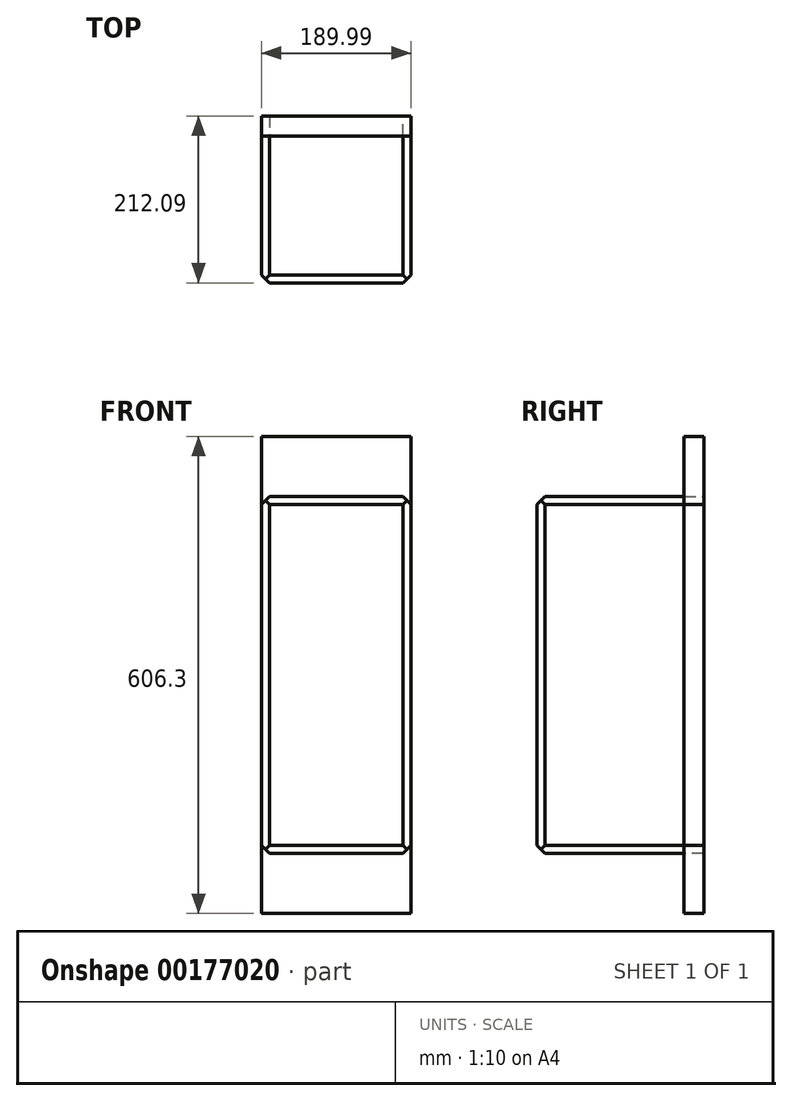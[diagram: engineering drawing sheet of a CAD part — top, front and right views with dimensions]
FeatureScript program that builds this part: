
annotation { "Feature Type Name" : "Feature", "Feature Type Description" : "" }
export const myFeature = defineFeature(function(context is Context, id is Id, definition is map)
    precondition{}
    {
        {
            var Q0;
            Q0=qCreatedBy(makeId("Front.planeOp"),FACE);
            var sketch = newSketch(context, id + "F0", { "sketchPlane" : qUnion([Q0])});
            skLineSegment(sketch, "E0.bottom", {"start": v(0, 0) * mm, "end": v(190, 0) * mm});
            skLineSegment(sketch, "E0.top", {"start": v(0, -453.9) * mm, "end": v(190, -453.9) * mm});
            skLineSegment(sketch, "E0.left", {"start": v(0, 0) * mm, "end": v(0, -453.9) * mm});
            skLineSegment(sketch, "E0.right", {"start": v(190, 0) * mm, "end": v(190, -453.9) * mm});
            skLineSegment(sketch, "E1.bottom", {"start": v(0, 76.2) * mm, "end": v(190, 76.2) * mm});
            skLineSegment(sketch, "E1.top", {"start": v(0, -530.1) * mm, "end": v(190, -530.1) * mm});
            skLineSegment(sketch, "E1.left", {"start": v(0, 76.2) * mm, "end": v(0, -530.1) * mm});
            skLineSegment(sketch, "E1.right", {"start": v(190, 76.2) * mm, "end": v(190, -530.1) * mm});
            skSolve(sketch);
        }
        {
            var Q0;
            Q0=makeQuery(id+"F0.imprint","IMPRINT",FACE,{"disambiguationData":[TD([[makeQuery(id+"F0.imprint","IMPRINT",EDGE,{"derivedFrom":sQuery(id+"F0.wireOp",EDGE,"E0.bottom")}),-1.0]])]});
            extrude(context, id + "F1", {"entities" : qUnion([Q0]), "depth" : 212.1 * mm});
        }
        {
            var Q0;
            Q0=makeQuery(id+"F1.opExtrude","SWEPT_EDGE",EDGE,{"disambiguationData":[OSD([sQuery(id+"F0.wireOp",EDGE,"E0.bottom"),sQuery(id+"F0.wireOp",EDGE,"E0.left")])]});
            var Q1;
            Q1=makeQuery(id+"F1.opExtrude","SWEPT_EDGE",EDGE,{"disambiguationData":[OSD([sQuery(id+"F0.wireOp",EDGE,"E0.bottom"),sQuery(id+"F0.wireOp",EDGE,"E0.right")])]});
            var Q2;
            Q2=makeQuery(id+"F1.opExtrude","SWEPT_EDGE",EDGE,{"disambiguationData":[OSD([sQuery(id+"F0.wireOp",EDGE,"E0.top"),sQuery(id+"F0.wireOp",EDGE,"E0.right")])]});
            var Q3;
            Q3=makeQuery(id+"F1.opExtrude","SWEPT_EDGE",EDGE,{"disambiguationData":[OSD([sQuery(id+"F0.wireOp",EDGE,"E0.top"),sQuery(id+"F0.wireOp",EDGE,"E0.left")])]});
            chamfer(context, id + "F2", {"entities" : qUnion([Q0, Q1, Q2, Q3]), "width" : 10.16 * mm});
        }
        {
            var Q0;
            Q0=makeQuery(id+"F1.opExtrude","CAP_EDGE",EDGE,{"disambiguationData":[OSD([sQuery(id+"F0.wireOp",EDGE,"E0.bottom")])],"isStart":false});
            var Q1;
            Q1=makeQuery(id+"F1.opExtrude","CAP_EDGE",EDGE,{"disambiguationData":[OSD([sQuery(id+"F0.wireOp",EDGE,"E0.left")])],"isStart":false});
            var Q2;
            Q2=makeQuery(id+"F1.opExtrude","CAP_EDGE",EDGE,{"disambiguationData":[OSD([sQuery(id+"F0.wireOp",EDGE,"E0.right")])],"isStart":false});
            var Q3;
            Q3=makeQuery(id+"F1.opExtrude","CAP_EDGE",EDGE,{"disambiguationData":[OSD([sQuery(id+"F0.wireOp",EDGE,"E0.top")])],"isStart":false});
            chamfer(context, id + "F3", {"entities" : qUnion([Q0, Q1, Q2, Q3]), "width" : 10.16 * mm, "tangentPropagation" : true});
        }
        {
            var Q0;
            {var subQ0=sQuery(id+"F0.wireOp",EDGE,"E0.bottom");Q0=makeQuery(id+"F0.imprint","IMPRINT",FACE,{"disambiguationData":[TD([[makeQuery(id+"F0.imprint","IMPRINT",EDGE,{"derivedFrom":subQ0}),1.0]])]});}
            var Q1;
            {var subQ0=sQuery(id+"F0.wireOp",EDGE,"E0.top");Q1=makeQuery(id+"F0.imprint","IMPRINT",FACE,{"disambiguationData":[TD([[makeQuery(id+"F0.imprint","IMPRINT",EDGE,{"derivedFrom":subQ0}),-1.0]])]});}
            var Q2;
            {var subQ0=sQuery(id+"F0.wireOp",EDGE,"E0.bottom");Q2=makeQuery(id+"F0.imprint","IMPRINT",FACE,{"disambiguationData":[TD([[makeQuery(id+"F0.imprint","IMPRINT",EDGE,{"derivedFrom":subQ0}),-1.0]])]});}
            extrude(context, id + "F4", {"entities" : qUnion([Q0, Q1, Q2]), "depth" : 25.4 * mm});
        }
    });
